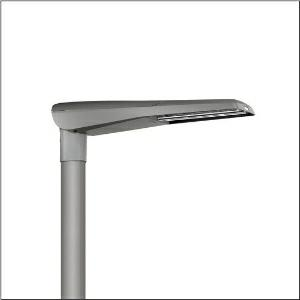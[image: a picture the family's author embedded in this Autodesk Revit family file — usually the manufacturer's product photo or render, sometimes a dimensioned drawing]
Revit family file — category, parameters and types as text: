
# Revit family: streetlight_sl_11_iq_mini___st1_2a_5xc2ac1f08he_c396
name_source: partatom
category: Lighting Fixtures
units: mm (PartAtom-declared; Revit-internal decimal feet)

## family parameters
Cut with Voids When Loaded = No
Host = Face
Light Source = No
Part Type = Normal
Room Calculation Point = No
Round Connector Dimension = Use Diameter
Shared = No

## types (1)
- --- (1 x LED, 6820 lm, 63.6 W, 2200K)
    Apparent Load = 64 VA
    CIE Flux Codes = 32 70 96 100 100
    Color Rendering = 70
    Color Temperature = 2200K
    Default Elevation = 1800 mm
    Description = Streetlight SL 11 iQ mini, mast luminaire, primary light control with 3 zone facetted reflector, of plastic, silver coated, highly specular, primary optical cover: cover, of PMMA, transparent, light distribution: ST1.2a, light emission: direct distribution, primary light characteristic: asymmetric, installation type: post-top, side-entry, lamps: LED, High Power LED, rated values: 8.330lm | 62,2W | 133,9lm/W (begin service life); end service life: 8.330lm | 65,6W; at 50% lumin. flux: 4.165lm | 29,4W | 141,7lm/W, colour temperature: 2200/2700/3000/4000K, colour rendering: CRI > 70, light colour: 722/727/730/740, light setting 1 begin service life: 100% | 8.330lm | 62,2W | 133,9lm/W | 3.000K, light setting 1 end service life: 65,6W, further light settings possible, control: Street-Remote, Auto-Match, Temp-Guard, Lumen-Switch, Night-Set, Smart-Wire, Light-Fading, Desk-Remote (wireless, voltage-free reading and setting of iQ features in the workshop via application-optimized NFC function/RFID function), optimised constant luminous flux control (CLO 2.0), with cable H07RN-F 3x 1.5mm², mains connection: 230..240V, AC, 50/60Hz, connection cable pre-assembled, cable length: 8,5m, luminaire housing, of diecast aluminium, powder-coated, SITECO metallic grey (DB 702S), please order mast flange separately, inclination adjustable without tools: 0°, 5°, 10°, 15° (post-top) | 0°, -5°, -10°, -15° (side-entry), sealing non-destructively replaceable, multi-level sealing system, length: 736mm, width: 174mm, height: 116mm, mast flange for spigot size: 42mm (side-entry): 5XC10008XM4, 60/48mm (side-entry/post-top): 5XC10108XM2, 76/60mm (side-entry/post-top): 5XC10108XM1, equipment: Power, protection rating (complete): IP66, insulation class (complete): insulation class II (safety insulation), certification: CE, ENEC, ENEC+, VDE, impact resistance: IK10, permissible operating ambient temperature for outdoor applications: -25..+50°C, standard-compliant lighting for roads and squares, Environmental Product Declaration (EPD) tested and certified by an independent institute, packaging unit: 1 piece

Light Distribution: ST1.2a
    Height = 116 mm
    Lamp = 1 x LED
    Lamp Light Flux = 6820 lm
    Lamp Power = 63.6 W
    Lamp count = 1
    Length = 736 mm
    Luminous efficacy = 107 lm/W
    Manufacturer = Siteco
    ModVariant = No
    Model = 5XC2AC1F08HE
    Number of Poles = 1
    OnlyDefault = Yes
    Power Factor = 1
    Product Name = Streetlight SL 11 iQ mini | ST1.2a
    Product group = mast luminaire | pylon top
    ProductGroupID = 6100
    Protection Class = Protection class II
    Protection Degree = IP 66
    RLX_Detail_Level = 1
    RLX_Emergency_Light_Flux = 0 lm
    RLX_Emergency_Type = 0
    RLX_Emergency_Type_DB = No
    RlxData = <blob elided: 53817 chars, md5=60967540>
    Socket = socket
    Standby Power = 0 W
    System Light Flux = 6820 lm
    System Power = 64 W
    Type Comments = individual setting: luminous flux: 100 % | dim-lin: 254 | 866 mA
    Type Image = l_1003508.jpg
    URL = http://relux.com
    VarID = @adj_041679
    Voltage = 0 V
    Weight = 0.00 kg
    Width = 174 mm

## geometry (parser evidence)
native form markers: Blend x4, Sweep x11
no freeform markers — native parametric forms only
